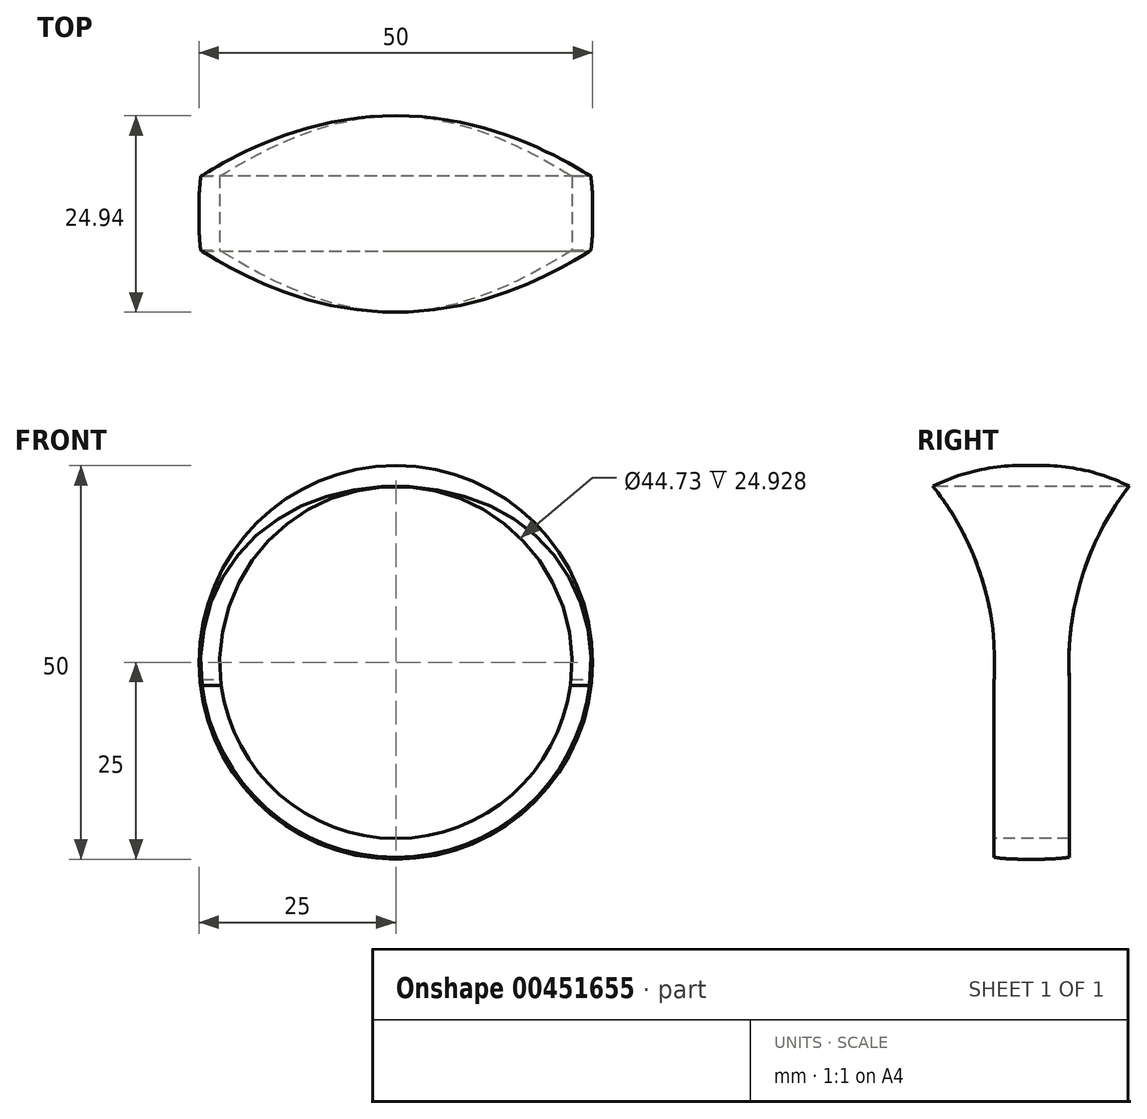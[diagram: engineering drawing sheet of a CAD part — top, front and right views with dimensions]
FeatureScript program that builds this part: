
annotation { "Feature Type Name" : "Feature", "Feature Type Description" : "" }
export const myFeature = defineFeature(function(context is Context, id is Id, definition is map)
    precondition{}
    {
        {
            var Q0;
            Q0=qCreatedBy(makeId("Front.planeOp"),FACE);
            var sketch = newSketch(context, id + "F0", { "sketchPlane" : qUnion([Q0])});
            skCircle(sketch, "E0", {"center": v(0, 0) * mm, "radius": 25 * mm});
            skSolve(sketch);
        }
        {
            var Q0;
            Q0 = qSketchRegion(id + "F0", true);
            extrude(context, id + "F1", {"entities" : qUnion([Q0]), "depth" : 25 * mm});
        }
        {
            var Q0;
            Q0=makeQuery(id+"F1.opExtrude","CAP_FACE",FACE,{"disambiguationData":[OSD([sQuery(id+"F0.wireOp",EDGE,"E0")])],"isStart":false});
            var sketch = newSketch(context, id + "F2", { "sketchPlane" : qUnion([Q0])});
            skCircle(sketch, "E1", {"center": v(0, 0) * mm, "radius": 22.37 * mm});
            skSolve(sketch);
        }
        {
            var Q0;
            Q0 = qSketchRegion(id + "F2", true);
            extrude(context, id + "F3", {"entities" : qUnion([Q0]), "operationType" : NewBodyOperationType.REMOVE, "endBound" : BoundingType.SYMMETRIC, "oppositeDirection" : true, "depth" : 64.4 * mm});
        }
        {
            var Q0;
            Q0=makeQuery(id+"F1.opExtrude","CAP_EDGE",EDGE,{"disambiguationData":[OSD([sQuery(id+"F0.wireOp",EDGE,"E0")])],"isStart":false});
            var Q1;
            Q1=makeQuery(id+"F1.opExtrude","CAP_EDGE",EDGE,{"disambiguationData":[OSD([sQuery(id+"F0.wireOp",EDGE,"E0")])],"isStart":true});
            fillet(context, id + "F4", {"entities" : qUnion([Q0, Q1]), "radius" : 24.87 * mm, "tangentPropagation" : true, "allowEdgeOverflow" : false});
        }
        {
            var Q0;
            Q0=qCreatedBy(makeId("Right.planeOp"),FACE);
            var sketch = newSketch(context, id + "F5", { "sketchPlane" : qUnion([Q0])});
            skCircle(sketch, "E2", {"center": v(28.84, 0) * mm, "radius": 36.54 * mm});
            skSolve(sketch);
        }
        {
            var Q0;
            Q0=makeQuery(id+"F5.imprint","IMPRINT",FACE,{"disambiguationData":[TD([[makeQuery(id+"F5.imprint","IMPRINT",EDGE,{"derivedFrom":sQuery(id+"F5.wireOp",EDGE,"E2")}),1.0]])]});
            extrude(context, id + "F6", {"entities" : qUnion([Q0]), "operationType" : NewBodyOperationType.REMOVE, "endBound" : BoundingType.SYMMETRIC, "oppositeDirection" : true, "depth" : 76.4 * mm});
        }
        {
            var Q0;
            Q0=qCreatedBy(makeId("Right.planeOp"),FACE);
            var sketch = newSketch(context, id + "F7", { "sketchPlane" : qUnion([Q0])});
            skCircle(sketch, "E3", {"center": v(-52.94, 0) * mm, "radius": 35.8 * mm});
            skSolve(sketch);
        }
        {
            var Q0;
            Q0 = qSketchRegion(id + "F7", true);
            extrude(context, id + "F8", {"entities" : qUnion([Q0]), "operationType" : NewBodyOperationType.REMOVE, "endBound" : BoundingType.SYMMETRIC, "oppositeDirection" : true, "depth" : 118.4 * mm});
        }
        {
            var Q0;
            Q0=qCreatedBy(makeId("Right.planeOp"),FACE);
            var sketch = newSketch(context, id + "F9", { "sketchPlane" : qUnion([Q0])});
            skLineSegment(sketch, "E4", {"start": v(-17.25, 0) * mm, "end": v(-17.25, -55.3) * mm});
            skLineSegment(sketch, "E5", {"start": v(-17.25, -55.3) * mm, "end": v(-33.58, -3.82) * mm});
            skLineSegment(sketch, "E6", {"start": v(-33.58, -3.82) * mm, "end": v(-17.25, 0) * mm});
            skLineSegment(sketch, "E7", {"start": v(-7.64, 0) * mm, "end": v(-7.64, -55.3) * mm});
            skLineSegment(sketch, "E8", {"start": v(-7.64, -55.3) * mm, "end": v(6.06, -21.6) * mm});
            skLineSegment(sketch, "E9", {"start": v(6.06, -21.6) * mm, "end": v(-7.64, 0) * mm});
            skSolve(sketch);
        }
        {
            var Q0;
            Q0=makeQuery(id+"F9.imprint","IMPRINT",FACE,{"disambiguationData":[TD([[makeQuery(id+"F9.imprint","IMPRINT",EDGE,{"derivedFrom":sQuery(id+"F9.wireOp",EDGE,"E7")}),1.0]])]});
            extrude(context, id + "F10", {"entities" : qUnion([Q0]), "operationType" : NewBodyOperationType.REMOVE, "endBound" : BoundingType.SYMMETRIC, "oppositeDirection" : true, "depth" : 73.4 * mm});
        }
        {
            var Q0;
            Q0=qCreatedBy(makeId("Right.planeOp"),FACE);
            var sketch = newSketch(context, id + "F11", { "sketchPlane" : qUnion([Q0])});
            skLineSegment(sketch, "E10", {"start": v(-17.25, 0) * mm, "end": v(-17.25, -55.57) * mm});
            skLineSegment(sketch, "E11", {"start": v(-17.25, -55.57) * mm, "end": v(-31.08, -9.48) * mm});
            skLineSegment(sketch, "E12", {"start": v(-31.08, -9.48) * mm, "end": v(-17.25, 0) * mm});
            skSolve(sketch);
        }
        {
            var Q0;
            Q0 = qSketchRegion(id + "F11", true);
            extrude(context, id + "F12", {"entities" : qUnion([Q0]), "operationType" : NewBodyOperationType.REMOVE, "endBound" : BoundingType.SYMMETRIC, "oppositeDirection" : true, "depth" : 104.4 * mm});
        }
    });
